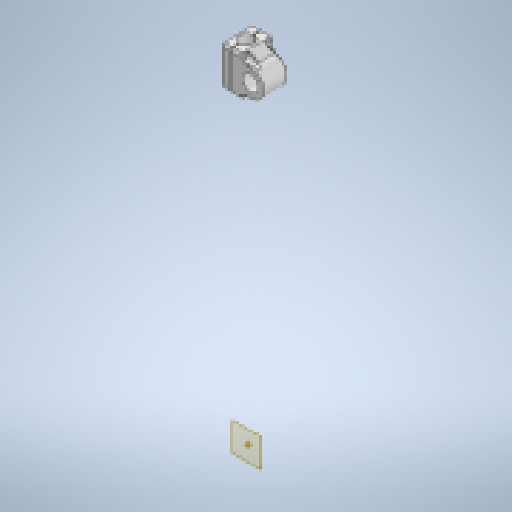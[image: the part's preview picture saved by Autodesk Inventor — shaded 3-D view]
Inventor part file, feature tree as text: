
AUTODESK INVENTOR PART (.ipt)
format: ipt  version: 2024.1 (Build 281209000, 209)  size: 527,872 bytes
history: native  units: mm
features: extrude x11, sketch x11, chamfer x9, other x7, projected_geometry x3, plane x2, fillet x2, reference x2
ambient origin geometry x8: Origin, YZ Plane, XZ Plane, XY Plane, X Axis, Y Axis, Z Axis, Center Point
bodies: Body1 (feature_tree), Body2 (feature_tree), Body3 (feature_tree)
feature tree (47):
  other  "clamp-top"
  plane  "Work Plane1"
  plane  "Work Plane2"
  extrude  "Extrusion1"  Depth=7.5mm
  extrude  "Extrusion2"  Depth=35.0mm TaperAngle=0.0deg
  extrude  "Extrusion3"  Depth=12.3mm
  chamfer  "Chamfer2"  Distance=30.0mm
  extrude  "Extrusion4"  Depth=4.7mm
  chamfer  "Chamfer3"  Distance=2.0mm Angle=45.0deg
  extrude  "Extrusion5"  Depth=3.2mm
  chamfer  "Chamfer4"  Distance=6.0mm
  extrude  "Extrusion7"  Depth=4.0mm
  extrude  "Extrusion6"  Depth=4.0mm
  fillet  "Fillet1"  Radius=3.5mm
  chamfer  "Chamfer9"  [1 undecoded]
  chamfer  "Chamfer10"  Distance=5.45mm
  extrude  "Extrusion8"  Depth=10.0mm TaperAngle=0.0deg
  chamfer  "Chamfer11"  Distance=2.0mm Angle=45.0deg
  chamfer  "Chamfer12"  Distance=6.0mm
  extrude  "Extrusion9"  Depth=4.0mm
  extrude  "Extrusion10"  Depth=4.0mm TaperAngle=45.0deg
  extrude  "Extrusion11"  Depth=4.0mm
  chamfer  "Chamfer13"  Distance=3.0mm
  fillet  "Fillet2"  Radius=0.3mm
  chamfer  "Chamfer1"  Distance=1.0mm
  other  "Work Point1"
  sketch  "Sketch2"  dims[d0=7.5mm d1=7.5mm]
  reference  "Reference1"
  sketch  "Sketch3"  dims[d2=2.0mm d3=35.0mm d4=0.0mm]
  sketch  "Sketch4"  dims[d5=0.25mm d6=12.3mm]
  projected_geometry  "Projected Loop1"
  projected_geometry  "Projected Loop2"
  projected_geometry  "Projected Loop3"
  sketch  "Sketch5"  dims[d7=6.0mm]
  sketch  "Sketch6"  dims[d9=4.0mm d10=30.0mm d11=0.0mm]
  sketch  "Sketch7"  dims[d12=0.0mm d13=0.0mm d14=4.7mm]
  other  "screw-cap"
  sketch  "Sketch8"  dims[d15=4.7mm d16=2.0mm d17=2.0mm d18=45.0deg]
  sketch  "Sketch9"  dims[d19=3.0mm d20=2.0mm d21=45.0deg d22=3.2mm]
  reference  "Reference2"
  other  "clamp-base"
  sketch  "Sketch10"  dims[d23=3.0mm]
  sketch  "Sketch11"  dims[d24=3.0mm]
  sketch  "Sketch12"  dims[d25=6.0mm d26=6.0mm d27=3.0mm d28=3.0mm d29=3.5mm d31=0.0mm d32=0.0mm d33=5.45mm d34=10.0mm d35=0.0mm d36=2.0mm d37=2.0mm d38=45.0deg d39=6.0mm d40=3.5mm d41=2.0mm d42=2.0mm d43=45.0deg d47=5.35mm d48=3.0mm d49=0.0mm d50=0.3mm d51=1.0mm d52=0.0mm d62=2.0mm d63=2.0mm d64=45.0deg d65=1.2mm d66=2.0mm d67=45.0deg d68=0.5mm d69=8.0mm d70=1.0mm d71=0.0mm d72=2.0mm d73=2.0mm d74=45.0deg d75=2.0mm d76=2.0mm d77=45.0deg d78=0.0mm d79=0.0mm d80=4.92mm d81=10.0mm d82=0.0mm d83=35.0mm d84=17.5mm d85=0.0mm d86=0.0mm d87=2.0mm d88=2.0mm d89=45.0deg d90=4.0mm]
  other  "<userpath>\Documents\0004-CAD\3D-cad-main\bike-rack\bike-rack-assembly.iam"
  other  "bike-rack-assembly.iam"
  other  "bike-rack:1"
note: 1 required parameter value undecoded (feature->parameter linkage not recoverable at this tier; creation-order binding heuristic only, values carry confidence <= 0.55)
